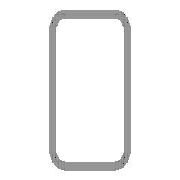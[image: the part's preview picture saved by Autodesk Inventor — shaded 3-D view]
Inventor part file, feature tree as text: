
AUTODESK INVENTOR PART (.ipt)
format: ipt  version: 2025.3 (Build 293356030, 356C)  size: 133,632 bytes
history: native  units: mm (DEFAULTED — no unit token found)
features: other x4, sketch x1, plane x1
ambient origin geometry x8: Origin, YZ Plane, XZ Plane, XY Plane, X Axis, Y Axis, Z Axis, Center Point
bodies: Solid1 (feature_tree), Body (feature_tree)
feature tree (6):
  parser-record x1  (decoder bookkeeping rows leaked as tree rows — omitted from the tree; the rows remain in map.json)
  other  "Driven Length"
  other  "Start Plane"
  other  "End Plane"
  sketch  "Sketch3"  dims[d3=200.0mm d4=0.0mm d7=4.0mm d9=20.0mm d11=40.0mm d12=2.0mm d13=-0.0mm d14=200.0mm d15=10.0mm d16=20.0mm d17=90.0deg d18=200.0mm]
  plane  "Work Plane3"
